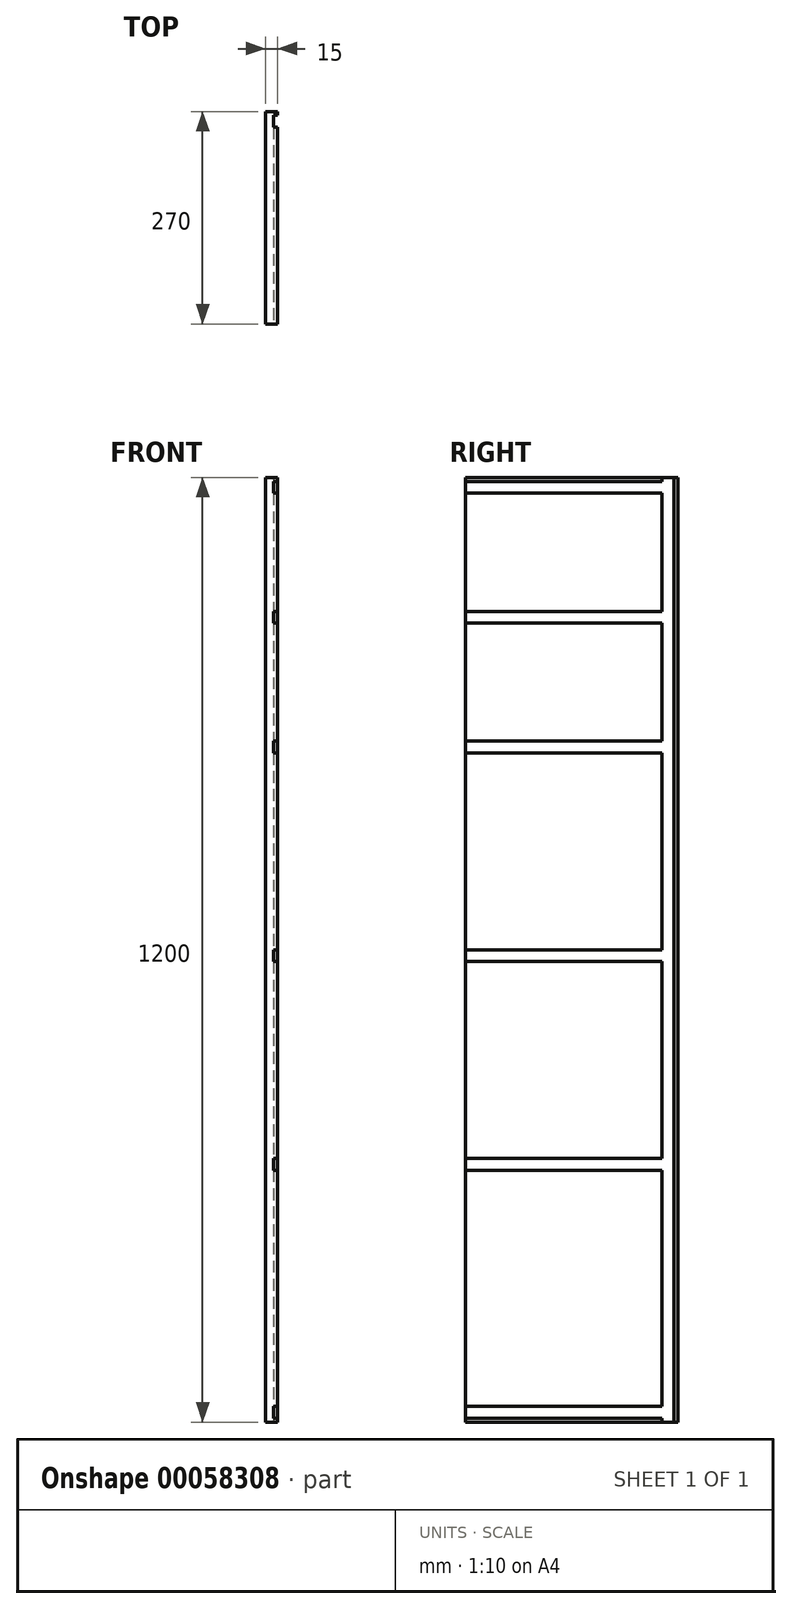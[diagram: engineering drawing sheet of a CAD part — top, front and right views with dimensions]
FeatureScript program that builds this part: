
annotation { "Feature Type Name" : "Feature", "Feature Type Description" : "" }
export const myFeature = defineFeature(function(context is Context, id is Id, definition is map)
    precondition{}
    {
        {
            var Q0;
            Q0=qCreatedBy(makeId("Right.planeOp"),FACE);
            var sketch = newSketch(context, id + "F0", { "sketchPlane" : qUnion([Q0])});
            skLineSegment(sketch, "E0.rect.bottom", {"start": v(135, -600) * mm, "end": v(-135, -600) * mm});
            skLineSegment(sketch, "E0.rect.top", {"start": v(135, 600) * mm, "end": v(-135, 600) * mm});
            skLineSegment(sketch, "E0.rect.left", {"start": v(135, -600) * mm, "end": v(135, 600) * mm});
            skLineSegment(sketch, "E0.rect.right", {"start": v(-135, -600) * mm, "end": v(-135, 600) * mm});
            skPoint(sketch, "E0.rect.middle", {"position": v(0, 0) * mm});
            skSolve(sketch);
        }
        {
            var Q0;
            Q0=makeQuery(id+"F0.imprint","IMPRINT",FACE,{"disambiguationData":[TD([[makeQuery(id+"F0.imprint","IMPRINT",EDGE,{"derivedFrom":sQuery(id+"F0.wireOp",EDGE,"E0.rect.bottom")}),-1.0]])]});
            extrude(context, id + "F1", {"entities" : qUnion([Q0]), "depth" : 15 * mm});
        }
        {
            var Q0;
            Q0=makeQuery(id+"F1.opExtrude","SWEPT_FACE",FACE,{"disambiguationData":[OSD([sQuery(id+"F0.wireOp",EDGE,"E0.rect.bottom")])]});
            var sketch = newSketch(context, id + "F2", { "sketchPlane" : qUnion([Q0])});
            skLineSegment(sketch, "E1.bottom", {"start": v(15, -130) * mm, "end": v(10, -130) * mm});
            skLineSegment(sketch, "E1.top", {"start": v(15, -115) * mm, "end": v(10, -115) * mm});
            skLineSegment(sketch, "E1.left", {"start": v(15, -130) * mm, "end": v(15, -115) * mm});
            skLineSegment(sketch, "E1.right", {"start": v(10, -130) * mm, "end": v(10, -115) * mm});
            skSolve(sketch);
        }
        {
            var Q0;
            Q0 = qSketchRegion(id + "F2", true);
            var Q1;
            Q1=makeQuery(id+"F1.opExtrude","SWEPT_FACE",FACE,{"disambiguationData":[OSD([sQuery(id+"F0.wireOp",EDGE,"E0.rect.top")])]});
            extrude(context, id + "F3", {"entities" : qUnion([Q0]), "operationType" : NewBodyOperationType.REMOVE, "endBound" : BoundingType.UP_TO_SURFACE, "oppositeDirection" : true, "endBoundEntityFace" : qUnion([Q1]), "depth" : 25 * mm});
        }
        {
            var Q0;
            Q0=makeQuery(id+"F1.opExtrude","SWEPT_FACE",FACE,{"disambiguationData":[OSD([sQuery(id+"F0.wireOp",EDGE,"E0.rect.right")])]});
            var sketch = newSketch(context, id + "F4", { "sketchPlane" : qUnion([Q0])});
            skLineSegment(sketch, "E2.bottom", {"start": v(15, -595) * mm, "end": v(10, -595) * mm});
            skLineSegment(sketch, "E2.top", {"start": v(15, -580) * mm, "end": v(10, -580) * mm});
            skLineSegment(sketch, "E2.left", {"start": v(15, -595) * mm, "end": v(15, -580) * mm});
            skLineSegment(sketch, "E2.right", {"start": v(10, -595) * mm, "end": v(10, -580) * mm});
            skLineSegment(sketch, "E3.bottom", {"start": v(15, -280) * mm, "end": v(10, -280) * mm});
            skLineSegment(sketch, "E3.top", {"start": v(15, -265) * mm, "end": v(10, -265) * mm});
            skLineSegment(sketch, "E3.left", {"start": v(15, -280) * mm, "end": v(15, -265) * mm});
            skLineSegment(sketch, "E3.right", {"start": v(10, -280) * mm, "end": v(10, -265) * mm});
            skLineSegment(sketch, "E4.bottom", {"start": v(15, -15) * mm, "end": v(10, -15) * mm});
            skLineSegment(sketch, "E4.top", {"start": v(15, 0) * mm, "end": v(10, 0) * mm});
            skLineSegment(sketch, "E4.left", {"start": v(15, -15) * mm, "end": v(15, 0) * mm});
            skLineSegment(sketch, "E4.right", {"start": v(10, -15) * mm, "end": v(10, 0) * mm});
            skLineSegment(sketch, "E5.bottom", {"start": v(15, 250) * mm, "end": v(10, 250) * mm});
            skLineSegment(sketch, "E5.top", {"start": v(15, 265) * mm, "end": v(10, 265) * mm});
            skLineSegment(sketch, "E5.left", {"start": v(15, 250) * mm, "end": v(15, 265) * mm});
            skLineSegment(sketch, "E5.right", {"start": v(10, 250) * mm, "end": v(10, 265) * mm});
            skLineSegment(sketch, "E6.bottom", {"start": v(15, 415) * mm, "end": v(10, 415) * mm});
            skLineSegment(sketch, "E6.top", {"start": v(15, 430) * mm, "end": v(10, 430) * mm});
            skLineSegment(sketch, "E6.left", {"start": v(15, 415) * mm, "end": v(15, 430) * mm});
            skLineSegment(sketch, "E6.right", {"start": v(10, 415) * mm, "end": v(10, 430) * mm});
            skLineSegment(sketch, "E7.bottom", {"start": v(15, 580) * mm, "end": v(10, 580) * mm});
            skLineSegment(sketch, "E7.top", {"start": v(15, 595) * mm, "end": v(10, 595) * mm});
            skLineSegment(sketch, "E7.left", {"start": v(15, 580) * mm, "end": v(15, 595) * mm});
            skLineSegment(sketch, "E7.right", {"start": v(10, 580) * mm, "end": v(10, 595) * mm});
            skSolve(sketch);
        }
        {
            var Q0;
            Q0 = qSketchRegion(id + "F4", true);
            var Q1;
            Q1=makeQuery(id+"F3.boolean.opBoolean","COPY",FACE,{"derivedFrom":makeQuery(id+"F3.opExtrude","SWEPT_FACE",FACE,{"disambiguationData":[OSD([sQuery(id+"F2.wireOp",EDGE,"E1.top")])]})});
            extrude(context, id + "F5", {"entities" : qUnion([Q0]), "operationType" : NewBodyOperationType.REMOVE, "endBound" : BoundingType.UP_TO_SURFACE, "oppositeDirection" : true, "endBoundEntityFace" : qUnion([Q1]), "depth" : 25 * mm});
        }
    });
